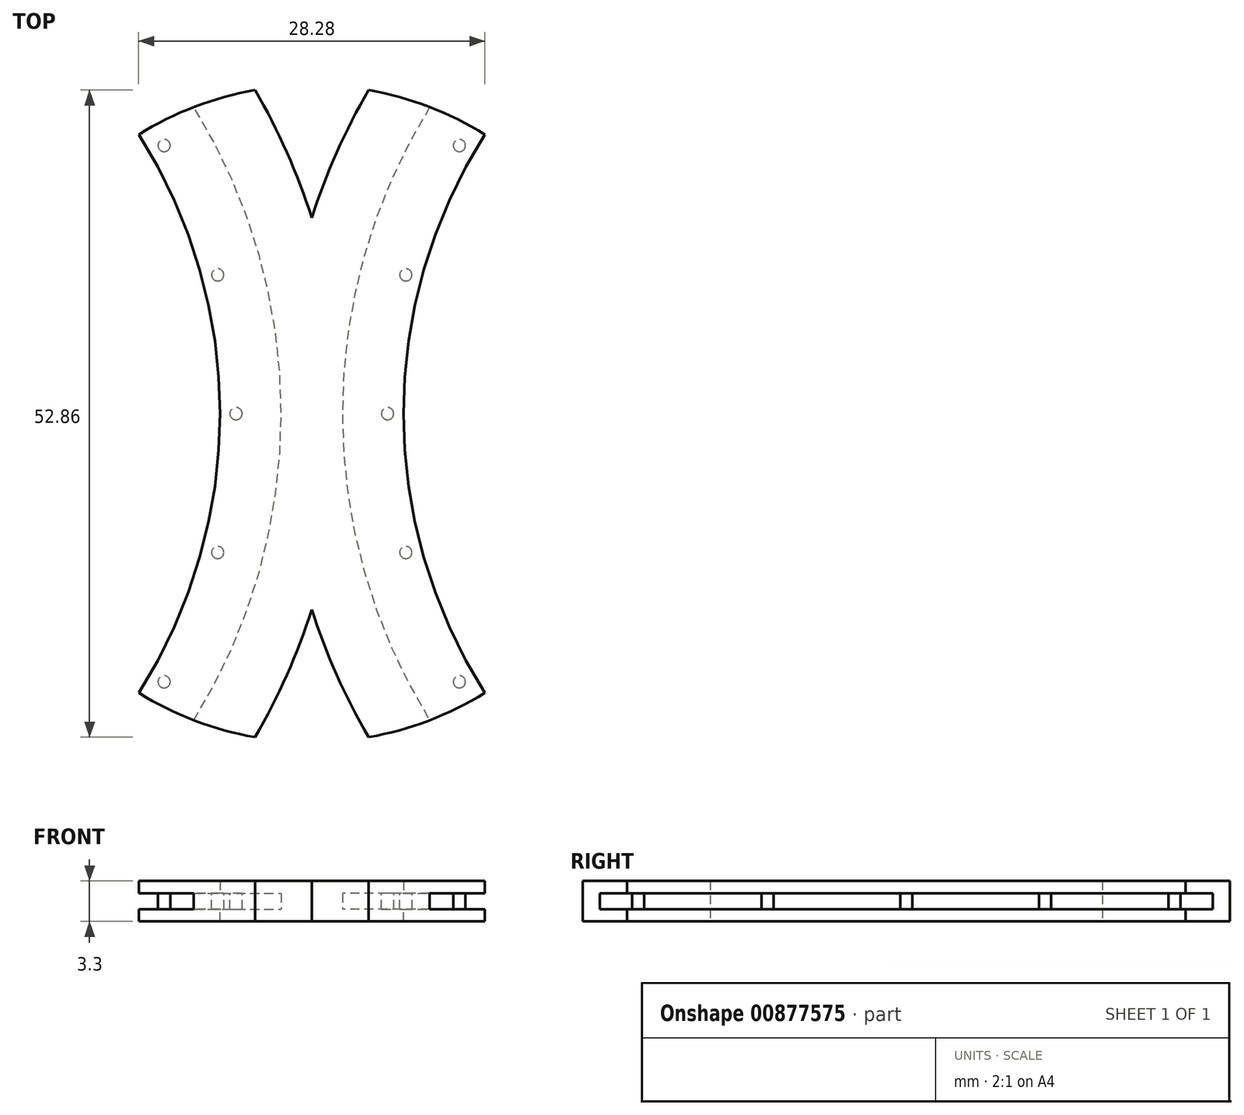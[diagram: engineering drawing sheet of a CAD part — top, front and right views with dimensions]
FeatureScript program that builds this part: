
annotation { "Feature Type Name" : "Feature", "Feature Type Description" : "" }
export const myFeature = defineFeature(function(context is Context, id is Id, definition is map)
    precondition{}
    {
        {
            var Q0;
            Q0=qCreatedBy(makeId("Top.planeOp"),FACE);
            var sketch = newSketch(context, id + "F0", { "sketchPlane" : qUnion([Q0])});
            skCircle(sketch, "E0.0", {"center": v(100, 0) * mm, "radius": 52.5 * mm});
            skLineSegment(sketch, "E1", {"start": v(47.5, 0) * mm, "end": v(52.5, 0) * mm, "construction": true});
            skPoint(sketch, "E2", {"position": v(50, 0) * mm});
            skCircle(sketch, "E3", {"center": v(0, 0) * mm, "radius": 42.5 * mm});
            skCircle(sketch, "E4", {"center": v(100, 0) * mm, "radius": 42.5 * mm});
            skArc(sketch, "E5", {"start": v(45.36, 26.43) * mm, "mid": v(40.44, 25.07) * mm, "end": v(35.86, 22.8) * mm});
            skArc(sketch, "E6", {"start": v(54.64, 26.43) * mm, "mid": v(50, 26.83) * mm, "end": v(45.36, 26.43) * mm, "construction": true});
            skArc(sketch, "E7", {"start": v(54.64, -26.43) * mm, "mid": v(59.56, -25.07) * mm, "end": v(64.14, -22.8) * mm});
            skArc(sketch, "E8", {"start": v(45.36, -26.43) * mm, "mid": v(50, -26.83) * mm, "end": v(54.64, -26.43) * mm, "construction": true});
            skArc(sketch, "E9", {"start": v(35.86, 22.8) * mm, "mid": v(23.17, 0) * mm, "end": v(35.86, -22.8) * mm, "construction": true});
            skArc(sketch, "E10", {"start": v(35.86, -22.8) * mm, "mid": v(40.44, -25.07) * mm, "end": v(45.36, -26.43) * mm});
            skArc(sketch, "E11", {"start": v(64.14, -22.8) * mm, "mid": v(76.83, 0) * mm, "end": v(64.14, 22.8) * mm, "construction": true});
            skArc(sketch, "E12", {"start": v(64.14, 22.8) * mm, "mid": v(59.56, 25.07) * mm, "end": v(54.64, 26.43) * mm});
            skArc(sketch, "E13", {"start": v(45.36, 26.43) * mm, "mid": v(-52.5, 0) * mm, "end": v(45.36, -26.43) * mm});
            skArc(sketch, "E14", {"start": v(45.36, -26.43) * mm, "mid": v(52.5, 0) * mm, "end": v(45.36, 26.43) * mm});
            skPoint(sketch, "E15", {"position": v(40.36, 25.04) * mm});
            skArc(sketch, "E16", {"start": v(40.36, -25.04) * mm, "mid": v(47.5, 0) * mm, "end": v(40.36, 25.04) * mm});
            skArc(sketch, "E17", {"start": v(40.36, 25.04) * mm, "mid": v(-47.5, 0) * mm, "end": v(40.36, -25.04) * mm, "construction": true});
            skArc(sketch, "E18", {"start": v(59.64, 25.04) * mm, "mid": v(52.5, 0) * mm, "end": v(59.64, -25.04) * mm});
            skArc(sketch, "E19", {"start": v(59.64, -25.04) * mm, "mid": v(147.5, 0) * mm, "end": v(59.64, 25.04) * mm, "construction": true});
            skSolve(sketch);
        }
        {
            var Q0;
            {var subQ0=sQuery(id+"F0.wireOp",EDGE,"E12");var subQ1=sQuery(id+"F0.wireOp",EDGE,"E0.0");var subQ2=makeQuery(id+"F0.imprint","INTERSECT",VERTEX,{"derivedFrom":[subQ1,subQ0]});Q0=makeQuery(id+"F0.imprint","IMPRINT",FACE,{"disambiguationData":[TD([[makeQuery(id+"F0.imprint","IMPRINT",EDGE,{"disambiguationData":[TD([[subQ2,-1.0]])],"derivedFrom":subQ1}),1.0]])]});}
            var Q1;
            {var subQ0=sQuery(id+"F0.wireOp",EDGE,"E14");var subQ1=sQuery(id+"F0.wireOp",EDGE,"E0.0");var subQ2=makeQuery(id+"F0.imprint","INTERSECT",VERTEX,{"disambiguationData":[OD(0.0)],"derivedFrom":[subQ1,subQ0]});Q1=makeQuery(id+"F0.imprint","IMPRINT",FACE,{"disambiguationData":[TD([[makeQuery(id+"F0.imprint","IMPRINT",EDGE,{"disambiguationData":[TD([[subQ2,-1.0]])],"derivedFrom":subQ1}),-1.0]])]});}
            var Q2;
            {var subQ0=sQuery(id+"F0.wireOp",EDGE,"E14");var subQ1=sQuery(id+"F0.wireOp",EDGE,"E0.0");var subQ2=makeQuery(id+"F0.imprint","INTERSECT",VERTEX,{"disambiguationData":[OD(1.0)],"derivedFrom":[subQ1,subQ0]});Q2=makeQuery(id+"F0.imprint","IMPRINT",FACE,{"disambiguationData":[TD([[makeQuery(id+"F0.imprint","IMPRINT",EDGE,{"disambiguationData":[TD([[subQ2,1.0]])],"derivedFrom":subQ1}),-1.0]])]});}
            var Q3;
            {var subQ0=sQuery(id+"F0.wireOp",EDGE,"E7");var subQ1=sQuery(id+"F0.wireOp",EDGE,"E0.0");var subQ2=makeQuery(id+"F0.imprint","INTERSECT",VERTEX,{"derivedFrom":[subQ1,subQ0]});Q3=makeQuery(id+"F0.imprint","IMPRINT",FACE,{"disambiguationData":[TD([[makeQuery(id+"F0.imprint","IMPRINT",EDGE,{"disambiguationData":[TD([[subQ2,1.0]])],"derivedFrom":subQ1}),1.0]])]});}
            var Q4;
            {var subQ0=sQuery(id+"F0.wireOp",EDGE,"E14");var subQ1=sQuery(id+"F0.wireOp",EDGE,"E0.0");var subQ2=makeQuery(id+"F0.imprint","INTERSECT",VERTEX,{"disambiguationData":[OD(0.0)],"derivedFrom":[subQ1,subQ0]});Q4=makeQuery(id+"F0.imprint","IMPRINT",FACE,{"disambiguationData":[TD([[makeQuery(id+"F0.imprint","IMPRINT",EDGE,{"disambiguationData":[TD([[subQ2,-1.0]])],"derivedFrom":subQ1}),1.0]])]});}
            extrude(context, id + "F1", {"entities" : qUnion([Q0, Q1, Q2, Q3, Q4]), "endBound" : BoundingType.SYMMETRIC, "depth" : 1.3 * mm, "offsetDistance" : 25 * mm});
        }
        {
            var Q0;
            Q0=makeQuery(id+"F1.opExtrude","CAP_FACE",FACE,{"disambiguationData":[OSD([sQuery(id+"F0.wireOp",EDGE,"E0.0"),sQuery(id+"F0.wireOp",EDGE,"E5"),sQuery(id+"F0.wireOp",EDGE,"E7"),sQuery(id+"F0.wireOp",EDGE,"E10"),sQuery(id+"F0.wireOp",EDGE,"E12"),sQuery(id+"F0.wireOp",EDGE,"E14"),sQuery(id+"F0.wireOp",EDGE,"E16"),sQuery(id+"F0.wireOp",EDGE,"E18")])],"isStart":true});
            var sketch = newSketch(context, id + "F2", { "sketchPlane" : qUnion([Q0])});
            skArc(sketch, "E20.0.0", {"start": v(40.36, -25.04) * mm, "mid": v(38.06, -24.03) * mm, "end": v(35.86, -22.8) * mm});
            skArc(sketch, "E20.0.1", {"start": v(35.86, -22.8) * mm, "mid": v(42.5, 0) * mm, "end": v(35.86, 22.8) * mm});
            skArc(sketch, "E20.0.2", {"start": v(35.86, 22.8) * mm, "mid": v(38.06, 24.03) * mm, "end": v(40.36, 25.04) * mm});
            skArc(sketch, "E20.0.3", {"start": v(40.36, 25.04) * mm, "mid": v(45.68, 13.02) * mm, "end": v(47.5, 0) * mm});
            skArc(sketch, "E20.0.4", {"start": v(47.5, 0) * mm, "mid": v(45.68, -13.02) * mm, "end": v(40.36, -25.04) * mm});
            skArc(sketch, "E21.0.0", {"start": v(64.14, 22.8) * mm, "mid": v(57.5, 0) * mm, "end": v(64.14, -22.8) * mm});
            skArc(sketch, "E21.0.1", {"start": v(64.14, -22.8) * mm, "mid": v(61.94, -24.03) * mm, "end": v(59.64, -25.04) * mm});
            skArc(sketch, "E21.0.2", {"start": v(59.64, -25.04) * mm, "mid": v(54.32, -13.02) * mm, "end": v(52.5, 0) * mm});
            skArc(sketch, "E21.0.3", {"start": v(52.5, 0) * mm, "mid": v(54.32, 13.02) * mm, "end": v(59.64, 25.04) * mm});
            skArc(sketch, "E21.0.4", {"start": v(59.64, 25.04) * mm, "mid": v(61.94, 24.03) * mm, "end": v(64.14, 22.8) * mm});
            skArc(sketch, "E22.0.0", {"start": v(50, -16) * mm, "mid": v(52.04, -21.35) * mm, "end": v(54.64, -26.43) * mm});
            skArc(sketch, "E22.0.1", {"start": v(54.64, -26.43) * mm, "mid": v(57.17, -25.86) * mm, "end": v(59.64, -25.04) * mm});
            skArc(sketch, "E22.0.2", {"start": v(59.64, -25.04) * mm, "mid": v(52.5, 0) * mm, "end": v(59.64, 25.04) * mm});
            skArc(sketch, "E22.0.3", {"start": v(59.64, 25.04) * mm, "mid": v(57.17, 25.86) * mm, "end": v(54.64, 26.43) * mm});
            skArc(sketch, "E22.0.4", {"start": v(54.64, 26.43) * mm, "mid": v(52.04, 21.35) * mm, "end": v(50, 16) * mm});
            skArc(sketch, "E22.0.5", {"start": v(50, 16) * mm, "mid": v(47.96, 21.35) * mm, "end": v(45.36, 26.43) * mm});
            skArc(sketch, "E22.0.6", {"start": v(45.36, 26.43) * mm, "mid": v(42.83, 25.86) * mm, "end": v(40.36, 25.04) * mm});
            skArc(sketch, "E22.0.7", {"start": v(40.36, 25.04) * mm, "mid": v(47.5, 0) * mm, "end": v(40.36, -25.04) * mm});
            skArc(sketch, "E22.0.8", {"start": v(40.36, -25.04) * mm, "mid": v(42.83, -25.86) * mm, "end": v(45.36, -26.43) * mm});
            skArc(sketch, "E22.0.9", {"start": v(45.36, -26.43) * mm, "mid": v(47.96, -21.35) * mm, "end": v(50, -16) * mm});
            skSolve(sketch);
        }
        {
            var Q0;
            Q0 = qSketchRegion(id + "F2", true);
            extrude(context, id + "F3", {"entities" : qUnion([Q0]), "operationType" : NewBodyOperationType.ADD, "depth" : 1 * mm, "offsetDistance" : 25 * mm});
        }
        {
            var Q0;
            Q0=makeQuery(id+"F1.opExtrude","SWEPT_BODY",BODY,{"disambiguationData":[OSD([sQuery(id+"F0.wireOp",EDGE,"E0.0"),sQuery(id+"F0.wireOp",EDGE,"E5"),sQuery(id+"F0.wireOp",EDGE,"E7"),sQuery(id+"F0.wireOp",EDGE,"E10"),sQuery(id+"F0.wireOp",EDGE,"E12"),sQuery(id+"F0.wireOp",EDGE,"E14"),sQuery(id+"F0.wireOp",EDGE,"E16"),sQuery(id+"F0.wireOp",EDGE,"E18")])]});
            var Q1;
            Q1=qCreatedBy(makeId("Top.planeOp"),FACE);
            mirror(context, id + "F4", {"operationType" : NewBodyOperationType.ADD, "entities" : qUnion([Q0]), "mirrorPlane" : qUnion([Q1])});
        }
        {
            var Q0;
            Q0=makeQuery(id+"F4.opPattern","COPY",FACE,{"derivedFrom":makeQuery(id+"F3.opExtrude","CAP_FACE",FACE,{"disambiguationData":[OSD([sQuery(id+"F2.wireOp",EDGE,"E20.0.0"),sQuery(id+"F2.wireOp",EDGE,"E20.0.1"),sQuery(id+"F2.wireOp",EDGE,"E20.0.2"),sQuery(id+"F2.wireOp",EDGE,"E21.0.0"),sQuery(id+"F2.wireOp",EDGE,"E21.0.1"),sQuery(id+"F2.wireOp",EDGE,"E21.0.4"),sQuery(id+"F2.wireOp",EDGE,"E22.0.0"),sQuery(id+"F2.wireOp",EDGE,"E22.0.1"),sQuery(id+"F2.wireOp",EDGE,"E22.0.3"),sQuery(id+"F2.wireOp",EDGE,"E22.0.4"),sQuery(id+"F2.wireOp",EDGE,"E22.0.5"),sQuery(id+"F2.wireOp",EDGE,"E22.0.6"),sQuery(id+"F2.wireOp",EDGE,"E22.0.8"),sQuery(id+"F2.wireOp",EDGE,"E22.0.9")])],"isStart":false}),"instanceName":"1"});
            var sketch = newSketch(context, id + "F5", { "sketchPlane" : qUnion([Q0])});
            skCircle(sketch, "E23", {"center": v(37.94, 21.9) * mm, "radius": 0.5 * mm});
            skCircle(sketch, "E24.1.0", {"center": v(42.32, 11.34) * mm, "radius": 0.5 * mm});
            skCircle(sketch, "E24.2.0", {"center": v(43.81, 0) * mm, "radius": 0.5 * mm});
            skCircle(sketch, "E24.3.0", {"center": v(42.32, -11.34) * mm, "radius": 0.5 * mm});
            skCircle(sketch, "E24.4.0", {"center": v(37.94, -21.9) * mm, "radius": 0.5 * mm});
            skPoint(sketch, "E24.center", {"position": v(0, 0) * mm});
            skLineSegment(sketch, "E24.anchor1", {"start": v(0, 0) * mm, "end": v(37.94, 21.9) * mm, "construction": true});
            skLineSegment(sketch, "E24.anchor2", {"start": v(0, 0) * mm, "end": v(37.94, -21.9) * mm, "construction": true});
            skLineSegment(sketch, "E25", {"start": v(50, 0) * mm, "end": v(50, 25.69) * mm, "construction": true});
            skCircle(sketch, "E26.MirrorC", {"center": v(62.06, 21.9) * mm, "radius": 0.5 * mm});
            skCircle(sketch, "E27.MirrorC", {"center": v(57.68, 11.34) * mm, "radius": 0.5 * mm});
            skCircle(sketch, "E28.MirrorC", {"center": v(56.19, 0) * mm, "radius": 0.5 * mm});
            skCircle(sketch, "E29.MirrorC", {"center": v(57.68, -11.34) * mm, "radius": 0.5 * mm});
            skCircle(sketch, "E30.MirrorC", {"center": v(62.06, -21.9) * mm, "radius": 0.5 * mm});
            skSolve(sketch);
        }
        {
            var Q0;
            Q0 = qSketchRegion(id + "F5", true);
            var Q1;
            Q1=makeQuery(id+"F3.opExtrude","CAP_FACE",FACE,{"disambiguationData":[OSD([sQuery(id+"F2.wireOp",EDGE,"E20.0.0"),sQuery(id+"F2.wireOp",EDGE,"E20.0.1"),sQuery(id+"F2.wireOp",EDGE,"E20.0.2"),sQuery(id+"F2.wireOp",EDGE,"E21.0.0"),sQuery(id+"F2.wireOp",EDGE,"E21.0.1"),sQuery(id+"F2.wireOp",EDGE,"E21.0.4"),sQuery(id+"F2.wireOp",EDGE,"E22.0.0"),sQuery(id+"F2.wireOp",EDGE,"E22.0.1"),sQuery(id+"F2.wireOp",EDGE,"E22.0.3"),sQuery(id+"F2.wireOp",EDGE,"E22.0.4"),sQuery(id+"F2.wireOp",EDGE,"E22.0.5"),sQuery(id+"F2.wireOp",EDGE,"E22.0.6"),sQuery(id+"F2.wireOp",EDGE,"E22.0.8"),sQuery(id+"F2.wireOp",EDGE,"E22.0.9")])],"isStart":false});
            extrude(context, id + "F6", {"entities" : qUnion([Q0]), "operationType" : NewBodyOperationType.ADD, "endBound" : BoundingType.UP_TO_SURFACE, "oppositeDirection" : true, "depth" : 25 * mm, "endBoundEntityFace" : qUnion([Q1]), "offsetDistance" : 25 * mm});
        }
    });
